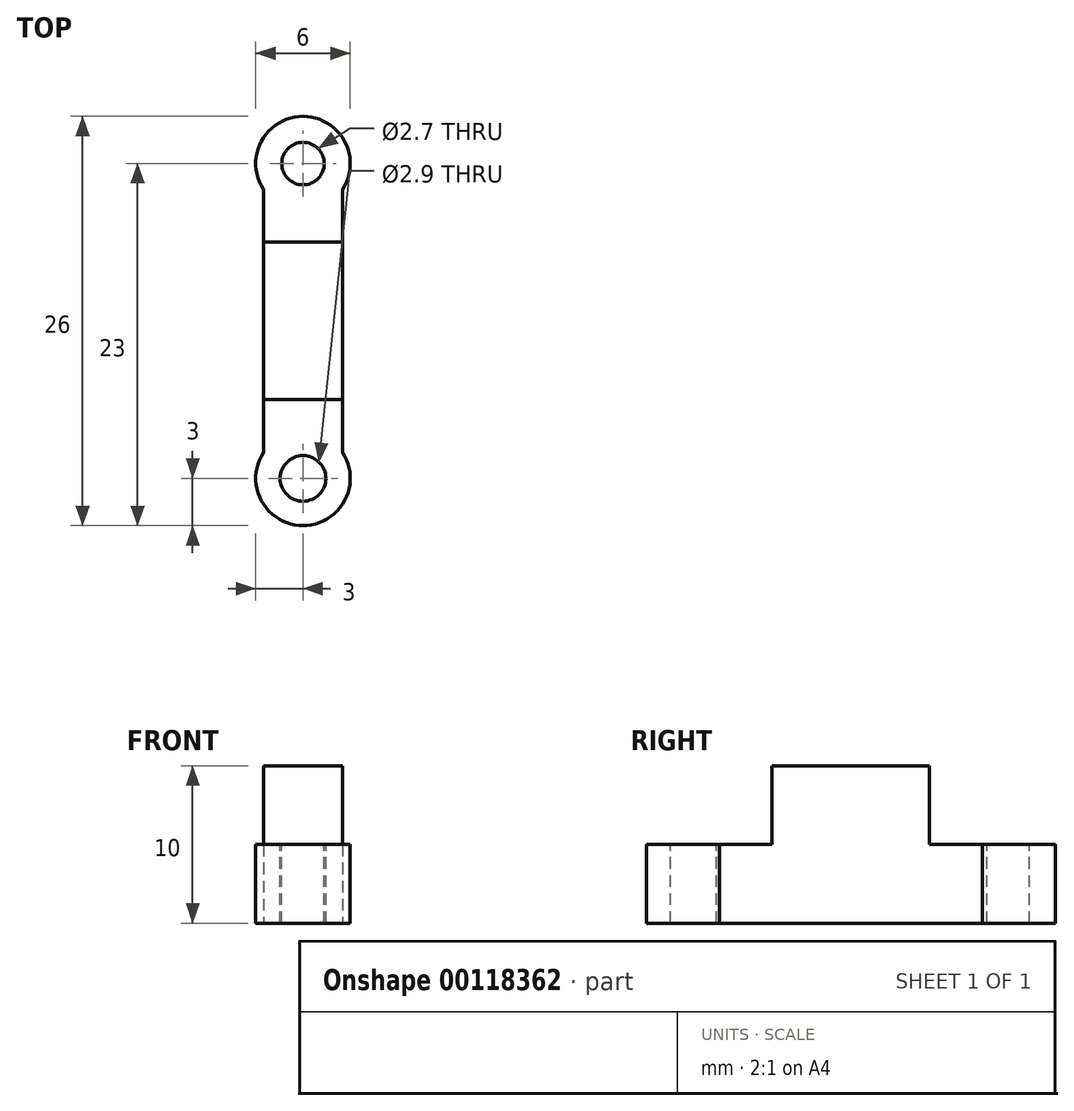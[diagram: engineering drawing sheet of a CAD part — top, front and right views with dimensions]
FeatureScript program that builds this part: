
annotation { "Feature Type Name" : "Feature", "Feature Type Description" : "" }
export const myFeature = defineFeature(function(context is Context, id is Id, definition is map)
    precondition{}
    {
        {
            var Q0;
            Q0=qCreatedBy(makeId("Top.planeOp"),FACE);
            var sketch = newSketch(context, id + "F0", { "sketchPlane" : qUnion([Q0])});
            skLineSegment(sketch, "E0.bottom", {"start": v(2.5, -10) * mm, "end": v(-2.5, -10) * mm});
            skLineSegment(sketch, "E0.top", {"start": v(2.5, 10) * mm, "end": v(-2.5, 10) * mm});
            skLineSegment(sketch, "E0.left", {"start": v(2.5, -10) * mm, "end": v(2.5, 10) * mm});
            skLineSegment(sketch, "E0.right", {"start": v(-2.5, -10) * mm, "end": v(-2.5, 10) * mm});
            skPoint(sketch, "E0.middle", {"position": v(0, 0) * mm});
            skSolve(sketch);
        }
        {
            var Q0;
            Q0=makeQuery(id+"F0.imprint","IMPRINT",FACE,{"disambiguationData":[TD([[makeQuery(id+"F0.imprint","IMPRINT",EDGE,{"derivedFrom":sQuery(id+"F0.wireOp",EDGE,"E0.bottom")}),-1.0]])]});
            extrude(context, id + "F1", {"entities" : qUnion([Q0]), "depth" : 5 * mm});
        }
        {
            var Q0;
            Q0=qCreatedBy(makeId("Top.planeOp"),FACE);
            var sketch = newSketch(context, id + "F2", { "sketchPlane" : qUnion([Q0])});
            skCircle(sketch, "E1", {"center": v(0, 10) * mm, "radius": 3 * mm});
            skSolve(sketch);
        }
        {
            var Q0;
            Q0 = qSketchRegion(id + "F2", true);
            extrude(context, id + "F3", {"entities" : qUnion([Q0]), "operationType" : NewBodyOperationType.ADD, "depth" : 5 * mm});
        }
        {
            var Q0;
            Q0=qCreatedBy(makeId("Top.planeOp"),FACE);
            var sketch = newSketch(context, id + "F4", { "sketchPlane" : qUnion([Q0])});
            skCircle(sketch, "E2", {"center": v(0, -10) * mm, "radius": 3 * mm});
            skSolve(sketch);
        }
        {
            var Q0;
            Q0 = qSketchRegion(id + "F4", true);
            extrude(context, id + "F5", {"entities" : qUnion([Q0]), "operationType" : NewBodyOperationType.ADD, "depth" : 5 * mm});
        }
        {
            var Q0;
            Q0=makeQuery(id+"F5.boolean.opBoolean","MERGE",FACE,{"derivedFrom":[makeQuery(id+"F3.boolean.opBoolean","MERGE",FACE,{"derivedFrom":[makeQuery(id+"F1.opExtrude","CAP_FACE",FACE,{"disambiguationData":[OSD([sQuery(id+"F0.wireOp",EDGE,"E0.bottom"),sQuery(id+"F0.wireOp",EDGE,"E0.top"),sQuery(id+"F0.wireOp",EDGE,"E0.left"),sQuery(id+"F0.wireOp",EDGE,"E0.right")])],"isStart":false}),makeQuery(id+"F3.opExtrude","CAP_FACE",FACE,{"disambiguationData":[OSD([sQuery(id+"F2.wireOp",EDGE,"E1")])],"isStart":false})]}),makeQuery(id+"F5.opExtrude","CAP_FACE",FACE,{"disambiguationData":[OSD([sQuery(id+"F4.wireOp",EDGE,"E2")])],"isStart":false})]});
            var sketch = newSketch(context, id + "F6", { "sketchPlane" : qUnion([Q0])});
            skCircle(sketch, "E3", {"center": v(0, 10) * mm, "radius": 1.35 * mm});
            skSolve(sketch);
        }
        {
            var Q0;
            Q0 = qSketchRegion(id + "F6", true);
            var Q1;
            Q1=sQuery(id+"F6.wireOp",EDGE,"E3");
            extrude(context, id + "F7", {"entities" : qUnion([Q0]), "operationType" : NewBodyOperationType.REMOVE, "surfaceEntities" : qUnion([Q1]), "oppositeDirection" : true, "depth" : 5 * mm});
        }
        {
            var Q0;
            Q0=makeQuery(id+"F5.boolean.opBoolean","MERGE",FACE,{"derivedFrom":[makeQuery(id+"F3.boolean.opBoolean","MERGE",FACE,{"derivedFrom":[makeQuery(id+"F1.opExtrude","CAP_FACE",FACE,{"disambiguationData":[OSD([sQuery(id+"F0.wireOp",EDGE,"E0.bottom"),sQuery(id+"F0.wireOp",EDGE,"E0.top"),sQuery(id+"F0.wireOp",EDGE,"E0.left"),sQuery(id+"F0.wireOp",EDGE,"E0.right")])],"isStart":false}),makeQuery(id+"F3.opExtrude","CAP_FACE",FACE,{"disambiguationData":[OSD([sQuery(id+"F2.wireOp",EDGE,"E1")])],"isStart":false})]}),makeQuery(id+"F5.opExtrude","CAP_FACE",FACE,{"disambiguationData":[OSD([sQuery(id+"F4.wireOp",EDGE,"E2")])],"isStart":false})]});
            var sketch = newSketch(context, id + "F8", { "sketchPlane" : qUnion([Q0])});
            skCircle(sketch, "E4", {"center": v(0, -10) * mm, "radius": 1.45 * mm});
            skSolve(sketch);
        }
        {
            var Q0;
            Q0 = qSketchRegion(id + "F8", true);
            extrude(context, id + "F9", {"entities" : qUnion([Q0]), "operationType" : NewBodyOperationType.REMOVE, "oppositeDirection" : true, "depth" : 5 * mm});
        }
        {
            var Q0;
            Q0=makeQuery(id+"F5.boolean.opBoolean","MERGE",FACE,{"derivedFrom":[makeQuery(id+"F3.boolean.opBoolean","MERGE",FACE,{"derivedFrom":[makeQuery(id+"F1.opExtrude","CAP_FACE",FACE,{"disambiguationData":[OSD([sQuery(id+"F0.wireOp",EDGE,"E0.bottom"),sQuery(id+"F0.wireOp",EDGE,"E0.top"),sQuery(id+"F0.wireOp",EDGE,"E0.left"),sQuery(id+"F0.wireOp",EDGE,"E0.right")])],"isStart":false}),makeQuery(id+"F3.opExtrude","CAP_FACE",FACE,{"disambiguationData":[OSD([sQuery(id+"F2.wireOp",EDGE,"E1")])],"isStart":false})]}),makeQuery(id+"F5.opExtrude","CAP_FACE",FACE,{"disambiguationData":[OSD([sQuery(id+"F4.wireOp",EDGE,"E2")])],"isStart":false})]});
            var sketch = newSketch(context, id + "F10", { "sketchPlane" : qUnion([Q0])});
            skLineSegment(sketch, "E5.bottom", {"start": v(2.5, -5) * mm, "end": v(-2.5, -5) * mm});
            skLineSegment(sketch, "E5.top", {"start": v(2.5, 5) * mm, "end": v(-2.5, 5) * mm});
            skLineSegment(sketch, "E5.left", {"start": v(2.5, -5) * mm, "end": v(2.5, 5) * mm});
            skLineSegment(sketch, "E5.right", {"start": v(-2.5, -5) * mm, "end": v(-2.5, 5) * mm});
            skPoint(sketch, "E5.middle", {"position": v(0, 0) * mm});
            skSolve(sketch);
        }
        {
            var Q0;
            Q0 = qSketchRegion(id + "F10", true);
            extrude(context, id + "F11", {"entities" : qUnion([Q0]), "operationType" : NewBodyOperationType.ADD, "depth" : 5 * mm});
        }
    });
